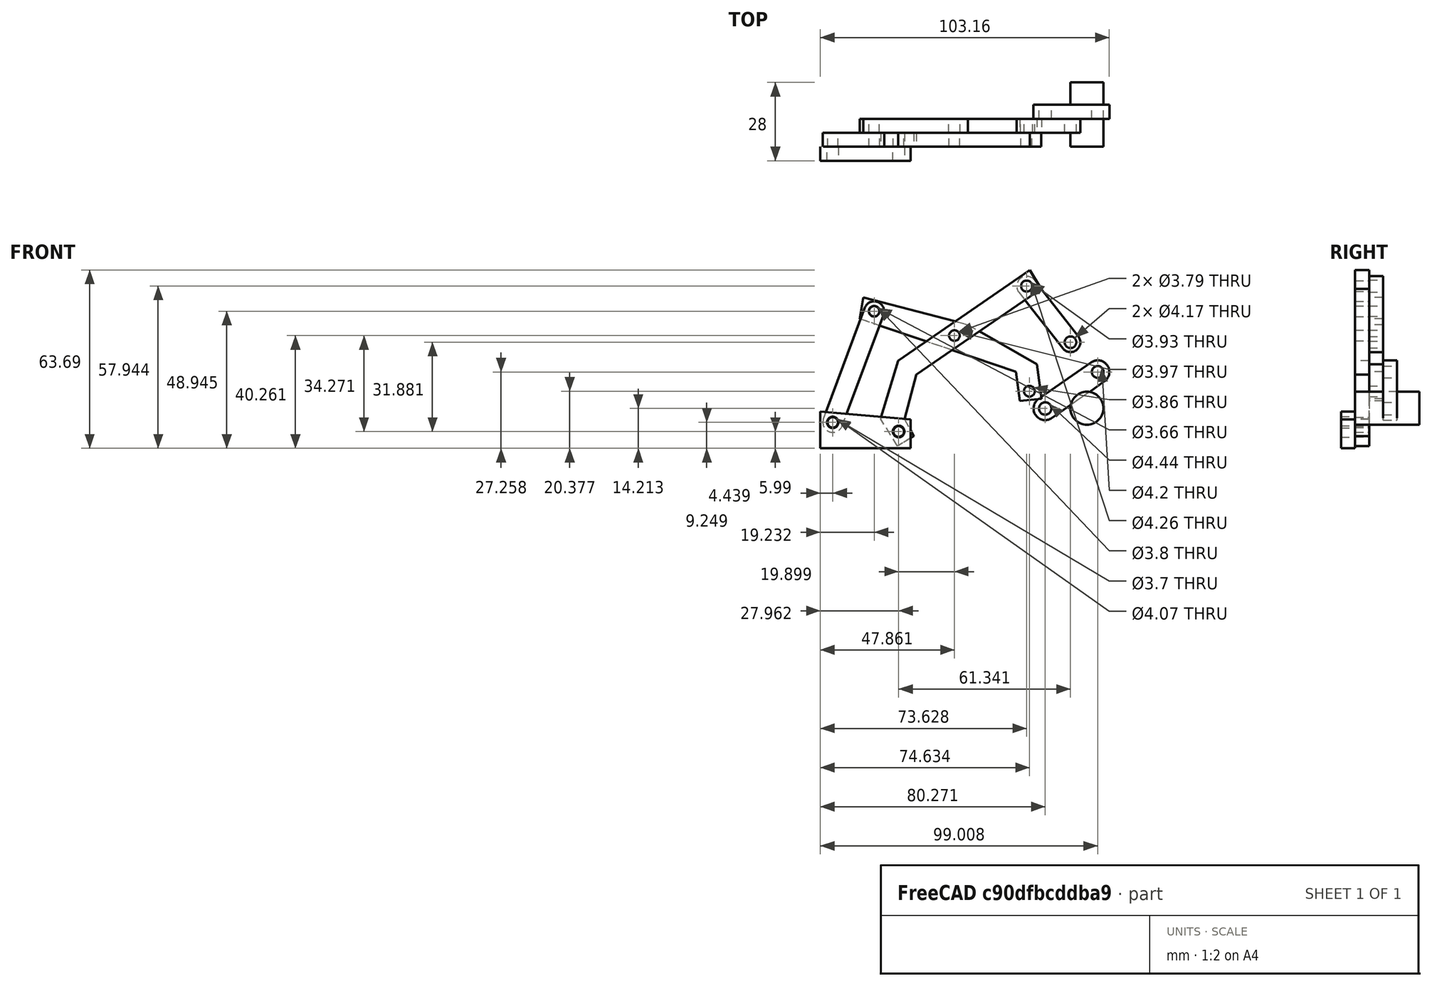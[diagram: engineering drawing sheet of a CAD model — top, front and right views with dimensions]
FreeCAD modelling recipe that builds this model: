
FCSTD DOCUMENT  (FreeCAD 1.1R14555 (Git shallow))
Label: TestMeca1-1
License: All rights reserved
LicenseURL: https://en.wikipedia.org/wiki/All_rights_reserved
objects: App::Point×11, App::FeaturePython×10, Sketcher::SketchObject×7, PartDesign::Pad×7, PartDesign::Body×7, App::Link×4, Assembly::JointGroup×2, Assembly::AssemblyObject×2, Image::ImagePlane×1, App::Part×1, Assembly::AssemblyLink×1
note: 42 computed .brp shape members not serialized (recipe doc carries the construction recipe); baked Part::Feature solids carry a one-line shape summary decoded from their .brp
EXTERNAL_REF file=TestInsert1-1.FCStd obj=Assembly
EXTERNAL_REF file=TestInsert1-1.FCStd obj=Body
EXTERNAL_REF file=TestInsert1-1.FCStd obj=Body001

FEATURE [App::Point] Origin001  label="Origine"
  Role = Origin
FEATURE [Image::ImagePlane] GN_7247_Charnière_articulée_drawing  label="GN 7247-Charnière articulée-drawing"
  Placement = pos=(-46,0,-26) rot=(1,0,0;1.5708rad)
  XSize = 264.55
  YSize = 264.55
FEATURE [App::Point] Origin003  label="Origine002"
  Role = Origin
FEATURE [Sketcher::SketchObject] Sketch
  ArcFitTolerance = 1e-06
  AttachmentSupport = -> [Origin002]
  ExternalTypes = [0]
  FullyConstrained = false
  MakeInternals = false
  MapMode = 5
  Placement = pos=(0,0,0) rot=(1,0,0;1.5708rad)
  sketch-geometry (6):
    g0: LineSegment StartX=0 StartY=0 StartZ=0 EndX=0 EndY=13.138 EndZ=0
    g1: LineSegment StartX=0 StartY=13.138 StartZ=0 EndX=32.2081 EndY=10.2743 EndZ=0
    g2: LineSegment StartX=32.2081 StartY=10.2743 StartZ=0 EndX=32.2081 EndY=0 EndZ=0
    g3: LineSegment StartX=32.2081 StartY=0 StartZ=0 EndX=0 EndY=0 EndZ=0
    g4: Circle CenterX=27.9622 CenterY=5.98985 CenterZ=0 NormalX=0 NormalY=0 NormalZ=1 AngleXU=0 Radius=2.08292
    g5: Circle CenterX=4.43862 CenterY=9.24882 CenterZ=0 NormalX=0 NormalY=0 NormalZ=1 AngleXU=0 Radius=2.03403
  constraints (8):
    c: Coincident(g-1,g0)
    c: PointOnObject(g0,g-2)
    c: Coincident(g0,g1)
    c: Coincident(g1,g2)
    c: PointOnObject(g2,g-1)
    c: Vertical(g2)
    c: Coincident(g2,g3)
    c: Coincident(g3,g0)
FEATURE [PartDesign::Pad] Pad
  Direction = (0,-1,0)
  Length = 5
  Length2 = 10
  Profile = -> Sketch
  ReferenceAxis = -> Sketch [N_Axis]
  Refine = true
  SideType = 0
  Suppressed = false
  Type = 0
  Type2 = 0
FEATURE [PartDesign::Body] Body  label="Corps"
  AllowCompound = false
  Group = -> [Sketch,Pad]
  Origin = -> Origin002
  Tip = -> Pad
FEATURE [App::Point] Origin005  label="Origine004"
  Role = Origin
FEATURE [Sketcher::SketchObject] Sketch001
  ArcFitTolerance = 1e-06
  AttachmentSupport = -> [Origin004]
  ExternalTypes = [0]
  FullyConstrained = false
  MakeInternals = false
  MapMode = 5
  Placement = pos=(0,0,0) rot=(1,0,0;1.5708rad)
  sketch-geometry (6):
    g0: ArcOfCircle CenterX=4.3933 CenterY=9.28745 CenterZ=0 NormalX=0 NormalY=0 NormalZ=1 AngleXU=0 Radius=3.55115 StartAngle=3.65377 EndAngle=6.79537
    g1: ArcOfCircle CenterX=-16.3679 CenterY=46.2142 CenterZ=0 NormalX=0 NormalY=0 NormalZ=1 AngleXU=0 Radius=3.55115 StartAngle=0.512182 EndAngle=3.65377
    g2: LineSegment StartX=1.29784 StartY=7.5471 StartZ=0 EndX=-19.4634 EndY=44.4739 EndZ=0
    g3: LineSegment StartX=7.48876 StartY=11.0278 StartZ=0 EndX=-13.2724 EndY=47.9545 EndZ=0
    g4: Circle CenterX=-16.3679 CenterY=46.2142 CenterZ=0 NormalX=0 NormalY=0 NormalZ=1 AngleXU=0 Radius=1.89824
    g5: Circle CenterX=4.3933 CenterY=9.28745 CenterZ=0 NormalX=0 NormalY=0 NormalZ=1 AngleXU=0 Radius=1.85066
  constraints (7):
    c: Tangent(g0,g2) = 1.5708
    c: Tangent(g0,g3) = -1.5708
    c: Tangent(g1,g2) = 1.5708
    c: Tangent(g1,g3) = -1.5708
    c: Equal(g0,g1)
    c: Coincident(g4,g1)
    c: Coincident(g5,g0)
FEATURE [PartDesign::Pad] Pad001
  Direction = (0,-1,2e-16)
  Length = 5
  Length2 = 10
  Profile = -> Sketch001
  ReferenceAxis = -> Sketch001 [N_Axis]
  Refine = true
  SideType = 0
  Suppressed = false
  Type = 0
  Type2 = 0
FEATURE [PartDesign::Body] Body001  label="Corps001"
  AllowCompound = false
  Group = -> [Sketch001,Pad001]
  Origin = -> Origin004
  Placement = pos=(-5.49004,5,6.60695) rot=(0,1,0;0.868892rad)
  Tip = -> Pad001
FEATURE [App::Point] Origin007  label="Origine006"
  Role = Origin
FEATURE [Sketcher::SketchObject] Sketch002
  ArcFitTolerance = 1e-06
  AttachmentSupport = -> [Origin006]
  ExternalTypes = [0]
  FullyConstrained = false
  MakeInternals = false
  MapMode = 5
  Placement = pos=(0,0,0) rot=(1,0,0;1.5708rad)
  sketch-geometry (6):
    g0: ArcOfCircle CenterX=9.93968 CenterY=74.2901 CenterZ=0 NormalX=0 NormalY=0 NormalZ=1 AngleXU=0 Radius=3.51304 StartAngle=0.499119 EndAngle=3.64071
    g1: ArcOfCircle CenterX=22.1303 CenterY=51.9285 CenterZ=0 NormalX=0 NormalY=0 NormalZ=1 AngleXU=0 Radius=3.51304 StartAngle=3.64071 EndAngle=6.7823
    g2: LineSegment StartX=13.0241 StartY=75.9716 StartZ=0 EndX=25.2148 EndY=53.61 EndZ=0
    g3: LineSegment StartX=6.85522 StartY=72.6086 StartZ=0 EndX=19.0458 EndY=50.247 EndZ=0
    g4: Circle CenterX=9.93968 CenterY=74.2901 CenterZ=0 NormalX=0 NormalY=0 NormalZ=1 AngleXU=0 Radius=2.12816
    g5: Circle CenterX=22.1303 CenterY=51.9285 CenterZ=0 NormalX=0 NormalY=0 NormalZ=1 AngleXU=0 Radius=2.08513
  constraints (7):
    c: Tangent(g0,g2) = 1.5708
    c: Tangent(g0,g3) = -1.5708
    c: Tangent(g1,g2) = 1.5708
    c: Tangent(g1,g3) = -1.5708
    c: Equal(g0,g1)
    c: Coincident(g4,g0)
    c: Coincident(g5,g1)
FEATURE [PartDesign::Pad] Pad002
  Direction = (0,-1,2e-16)
  Length = 5
  Length2 = 10
  Profile = -> Sketch002
  ReferenceAxis = -> Sketch002 [N_Axis]
  Refine = true
  SideType = 0
  Suppressed = false
  Type = 0
  Type2 = 0
FEATURE [PartDesign::Body] Body002  label="Corps002"
  AllowCompound = false
  Group = -> [Sketch002,Pad002]
  Origin = -> Origin006
  Placement = pos=(75.9415,10,-16.972) rot=(0,-1,0;0.16388rad)
  Tip = -> Pad002
FEATURE [App::Point] Origin009  label="Origine008"
  Role = Origin
FEATURE [Sketcher::SketchObject] Sketch003
  ArcFitTolerance = 1e-06
  AttachmentSupport = -> [Origin008]
  ExternalTypes = [0]
  FullyConstrained = false
  MakeInternals = false
  MapMode = 5
  Placement = pos=(0,0,0) rot=(1,0,0;1.5708rad)
  sketch-geometry (6):
    g0: ArcOfCircle CenterX=33.0045 CenterY=40.5366 CenterZ=0 NormalX=0 NormalY=0 NormalZ=1 AngleXU=0 Radius=4.15593 StartAngle=1e-16 EndAngle=3.14159
    g1: ArcOfCircle CenterX=33.0045 CenterY=17.7064 CenterZ=0 NormalX=0 NormalY=0 NormalZ=1 AngleXU=0 Radius=4.15593 StartAngle=3.14159 EndAngle=6.28319
    g2: LineSegment StartX=37.1605 StartY=40.5366 StartZ=0 EndX=37.1605 EndY=17.7064 EndZ=0
    g3: LineSegment StartX=28.8486 StartY=40.5366 StartZ=0 EndX=28.8486 EndY=17.7064 EndZ=0
    g4: Circle CenterX=33.0045 CenterY=40.5366 CenterZ=0 NormalX=0 NormalY=0 NormalZ=1 AngleXU=0 Radius=2.09794
    g5: Circle CenterX=33.0045 CenterY=17.7064 CenterZ=0 NormalX=0 NormalY=0 NormalZ=1 AngleXU=0 Radius=2.22145
  constraints (8):
    c: Tangent(g0,g2) = 1.5708
    c: Tangent(g0,g3) = -1.5708
    c: Tangent(g1,g2) = 1.5708
    c: Tangent(g1,g3) = -1.5708
    c: Equal(g0,g1)
    c: Vertical(g2)
    c: Coincident(g4,g0)
    c: Coincident(g5,g1)
FEATURE [PartDesign::Pad] Pad003
  Direction = (0,-1,0)
  Length = 5
  Length2 = 10
  Profile = -> Sketch003
  ReferenceAxis = -> Sketch003 [N_Axis]
  Refine = true
  SideType = 0
  Suppressed = false
  Type = 0
  Type2 = 0
FEATURE [PartDesign::Body] Body003  label="Corps003"
  AllowCompound = false
  Group = -> [Sketch003,Pad003]
  Origin = -> Origin008
  Placement = pos=(46.8816,15,31.1819) rot=(0,1,0;0.962596rad)
  Tip = -> Pad003
FEATURE [App::Point] Origin011  label="Origine010"
  Role = Origin
FEATURE [Sketcher::SketchObject] Sketch004
  ArcFitTolerance = 1e-06
  AttachmentSupport = -> [Origin010]
  ExternalTypes = [0]
  FullyConstrained = false
  MakeInternals = false
  MapMode = 5
  Placement = pos=(0,0,0) rot=(1,0,0;1.5708rad)
  sketch-geometry (10):
    g0: LineSegment StartX=-23.6072 StartY=51.3966 StartZ=0 EndX=-21.2757 EndY=58.8351 EndZ=0
    g1: LineSegment StartX=-21.2757 StartY=58.8351 StartZ=0 EndX=14.4735 EndY=44.1801 EndZ=0
    g2: LineSegment StartX=14.4735 StartY=44.1801 StartZ=0 EndX=37.011 EndY=26.9717 EndZ=0
    g3: LineSegment StartX=37.011 StartY=26.9717 StartZ=0 EndX=37.011 EndY=14.5372 EndZ=0
    g4: LineSegment StartX=37.011 StartY=14.5372 StartZ=0 EndX=29.2394 EndY=14.8702 EndZ=0
    g5: LineSegment StartX=29.2394 StartY=14.8702 StartZ=0 EndX=29.2394 EndY=25.3063 EndZ=0
    g6: LineSegment StartX=29.2394 StartY=25.3063 StartZ=0 EndX=-23.6072 EndY=51.3966 EndZ=0
    g7: Circle CenterX=33.061 CenterY=17.7892 CenterZ=0 NormalX=0 NormalY=0 NormalZ=1 AngleXU=0 Radius=1.92887
    g8: Circle CenterX=9.13695 CenterY=41.0232 CenterZ=0 NormalX=0 NormalY=0 NormalZ=1 AngleXU=0 Radius=1.9865
    g9: Circle CenterX=-18.1003 CenterY=53.3997 CenterZ=0 NormalX=0 NormalY=0 NormalZ=1 AngleXU=0 Radius=1.8317
  constraints (9):
    c: Coincident(g0,g1)
    c: Coincident(g1,g2)
    c: Coincident(g2,g3)
    c: Vertical(g3)
    c: Coincident(g3,g4)
    c: Coincident(g4,g5)
    c: Vertical(g5)
    c: Coincident(g5,g6)
    c: Coincident(g6,g0)
FEATURE [PartDesign::Pad] Pad004
  Direction = (0,-1,0)
  Length = 5
  Length2 = 10
  Profile = -> Sketch004
  ReferenceAxis = -> Sketch004 [N_Axis]
  Refine = true
  SideType = 0
  Suppressed = false
  Type = 0
  Type2 = 0
FEATURE [PartDesign::Body] Body004  label="Corps004"
  AllowCompound = false
  Group = -> [Sketch004,Pad004]
  Origin = -> Origin010
  Placement = pos=(44.202,10,-1.60818) rot=(0,-1,0;0.131988rad)
  Tip = -> Pad004
FEATURE [App::Point] Origin013  label="Origine012"
  Role = Origin
FEATURE [Sketcher::SketchObject] Sketch005
  ArcFitTolerance = 1e-06
  AttachmentSupport = -> [Origin012]
  ExternalTypes = [0]
  FullyConstrained = false
  MakeInternals = false
  MapMode = 5
  Placement = pos=(0,0,0) rot=(1,0,0;1.5708rad)
  sketch-geometry (11):
    g0: LineSegment StartX=3.31041 StartY=76.0954 StartZ=0 EndX=11.193 EndY=76.0954 EndZ=0
    g1: LineSegment StartX=11.193 StartY=76.0954 StartZ=0 EndX=13.8575 EndY=22.0275 EndZ=0
    g2: LineSegment StartX=13.8575 StartY=22.0275 StartZ=0 EndX=25.3278 EndY=10.0553 EndZ=0
    g3: LineSegment StartX=25.3278 StartY=10.0553 StartZ=0 EndX=32.1894 EndY=9.81025 EndZ=0
    g4: LineSegment StartX=32.1894 StartY=9.81025 StartZ=0 EndX=32.1894 EndY=2.90781 EndZ=0
    g5: LineSegment StartX=32.1894 StartY=2.90781 StartZ=0 EndX=20.7126 EndY=2.90781 EndZ=0
    g6: LineSegment StartX=20.7126 StartY=2.90781 StartZ=0 EndX=6.25418 EndY=19.1224 EndZ=0
    g7: LineSegment StartX=6.25418 StartY=19.1224 StartZ=0 EndX=3.31041 EndY=76.0954 EndZ=0
    g8: Circle CenterX=7.62181 CenterY=72.1475 CenterZ=0 NormalX=0 NormalY=0 NormalZ=1 AngleXU=0 Radius=1.96538
    g9: Circle CenterX=9.17842 CenterY=40.9348 CenterZ=0 NormalX=0 NormalY=0 NormalZ=1 AngleXU=0 Radius=1.89735
    g10: Circle CenterX=27.9374 CenterY=6.02718 CenterZ=0 NormalX=0 NormalY=0 NormalZ=1 AngleXU=0 Radius=1.89735
  constraints (11):
    c: Horizontal(g0)
    c: Coincident(g0,g1)
    c: Coincident(g1,g2)
    c: Coincident(g2,g3)
    c: Coincident(g3,g4)
    c: Vertical(g4)
    c: Coincident(g4,g5)
    c: Horizontal(g5)
    c: Coincident(g5,g6)
    c: Coincident(g6,g7)
    c: Coincident(g7,g0)
FEATURE [PartDesign::Pad] Pad005
  Direction = (0,-1,0)
  Length = 5
  Length2 = 10
  Profile = -> Sketch005
  ReferenceAxis = -> Sketch005 [N_Axis]
  Refine = true
  SideType = 0
  Suppressed = false
  Type = 0
  Type2 = 0
FEATURE [PartDesign::Body] Body005  label="Corps005"
  AllowCompound = false
  Group = -> [Sketch005,Pad005]
  Origin = -> Origin012
  Placement = pos=(8.18757,5,26.6245) rot=(0,1,0;1.01916rad)
  Tip = -> Pad005
FEATURE [App::FeaturePython] GroundedJoint  # Assembly grounded joint (typed FeaturePython)
  ObjectToGround = -> Body
FEATURE [App::FeaturePython] Joint  label="Revolute"  # Assembly joint (typed FeaturePython)
  Angle = 0
  AngleMax = 0
  AngleMin = 0
  Detach1 = false
  Detach2 = false
  Distance = 0
  Distance2 = 0
  EnableAngleMax = false
  EnableAngleMin = false
  EnableLengthMax = false
  EnableLengthMin = false
  JointType = 1 (Revolute)
  LengthMax = 0
  LengthMin = 0
  Placement1 = pos=(4.3933,-5,9.28745) rot=(1,0,0;1.5708rad)
  Placement2 = pos=(4.43862,0,9.24882) rot=(1,0,0;1.5708rad)
  Reference1 = -> Assembly [Body001.Edge18,Body001.Edge18]
  Reference2 = -> Assembly [Body.Edge17,Body.Edge17]
  Suppressed = false
FEATURE [App::FeaturePython] Joint001  label="Revolute001"  # Assembly joint (typed FeaturePython)
  Angle = 0
  AngleMax = 0
  AngleMin = 0
  Detach1 = false
  Detach2 = false
  Distance = 0
  Distance2 = 0
  EnableAngleMax = false
  EnableAngleMin = false
  EnableLengthMax = false
  EnableLengthMin = false
  JointType = 1 (Revolute)
  LengthMax = 0
  LengthMin = 0
  Placement1 = pos=(-16.3679,0,46.2142) rot=(1,0,0;1.5708rad)
  Placement2 = pos=(-18.1003,-5,53.3997) rot=(1,0,0;1.5708rad)
  Reference1 = -> Assembly [Body001.Edge14,Body001.Edge14]
  Reference2 = -> Assembly [Body004.Edge30,Body004.Edge30]
  Suppressed = false
FEATURE [App::FeaturePython] Joint002  label="Revolute002"  # Assembly joint (typed FeaturePython)
  Angle = 0
  AngleMax = 0
  AngleMin = 0
  Detach1 = false
  Detach2 = false
  Distance = 0
  Distance2 = 0
  EnableAngleMax = false
  EnableAngleMin = false
  EnableLengthMax = false
  EnableLengthMin = false
  JointType = 1 (Revolute)
  LengthMax = 0
  LengthMin = 0
  Placement1 = pos=(27.9374,-5,6.02718) rot=(1,0,0;1.5708rad)
  Placement2 = pos=(27.9622,0,5.98985) rot=(1,0,0;1.5708rad)
  Reference1 = -> Assembly [Body005.Edge33,Body005.Edge33]
  Reference2 = -> Assembly [Body.Edge14,Body.Edge14]
  Suppressed = false
FEATURE [App::FeaturePython] Joint005  label="Revolute005"  # Assembly joint (typed FeaturePython)
  Angle = 0
  AngleMax = 0
  AngleMin = 0
  Detach1 = false
  Detach2 = false
  Distance = 0
  Distance2 = 0
  EnableAngleMax = false
  EnableAngleMin = false
  EnableLengthMax = false
  EnableLengthMin = false
  JointType = 1 (Revolute)
  LengthMax = 0
  LengthMin = 0
  Placement1 = pos=(9.93968,-5,74.2901) rot=(1,0,0;1.5708rad)
  Placement2 = pos=(7.62181,0,72.1475) rot=(1,0,0;1.5708rad)
  Reference1 = -> Assembly [Body002.Edge15,Body002.Edge15]
  Reference2 = -> Assembly [Body005.Edge26,Body005.Edge26]
  Suppressed = false
FEATURE [App::FeaturePython] Joint006  label="Revolute006"  # Assembly joint (typed FeaturePython)
  Angle = 0
  AngleMax = 0
  AngleMin = 0
  Detach1 = false
  Detach2 = false
  Distance = 0
  Distance2 = 0
  EnableAngleMax = false
  EnableAngleMin = false
  EnableLengthMax = false
  EnableLengthMin = false
  JointType = 1 (Revolute)
  LengthMax = 0
  LengthMin = 0
  Placement1 = pos=(9.13695,-5,41.0232) rot=(1,0,0;1.5708rad)
  Placement2 = pos=(9.17842,0,40.9348) rot=(1,0,0;1.5708rad)
  Reference1 = -> Assembly [Body004.Edge24,Body004.Edge24]
  Reference2 = -> Assembly [Body005.Edge29,Body005.Edge29]
  Suppressed = false
FEATURE [App::Point] Origin015  label="Origine014"
  Role = Origin
FEATURE [App::Point] Origin017  label="Origine016"
  Role = Origin
FEATURE [Sketcher::SketchObject] Sketch006
  ArcFitTolerance = 1e-06
  AttachmentSupport = -> [Origin016]
  ExternalTypes = [0]
  FullyConstrained = false
  MakeInternals = false
  MapMode = 5
  Placement = pos=(0,0,0) rot=(1,0,0;1.5708rad)
  sketch-geometry (1):
    g0: Circle CenterX=95.172 CenterY=14.315 CenterZ=0 NormalX=0 NormalY=0 NormalZ=1 AngleXU=0 Radius=5.91026
FEATURE [PartDesign::Pad] Pad006
  Direction = (0,-1,2e-16)
  Length = 23
  Length2 = 10
  Profile = -> Sketch006
  ReferenceAxis = -> Sketch006 [N_Axis]
  Refine = true
  Reversed = true
  SideType = 0
  Suppressed = false
  Type = 0
  Type2 = 0
FEATURE [PartDesign::Body] Body006  label="Corps006"
  AllowCompound = false
  Group = -> [Sketch006,Pad006]
  Origin = -> Origin016
  Tip = -> Pad006
FEATURE [App::Part] Part
  Group = -> [Body003,Body006]
  Origin = -> Origin014
FEATURE [App::Point] Origin019  label="Origine018"
  Role = Origin
FEATURE [App::Link] Corps003
  LinkPlacement = pos=(77,-8.82149e-06,-4.76837e-07) rot=(0,0,1;0rad)
  LinkedObject = -> Body003
  Placement = pos=(77,-8.82149e-06,-4.76837e-07) rot=(0,0,1;0rad)
FEATURE [App::Link] Corps006
  LinkPlacement = pos=(14.8325,-13,14.8956) rot=(0,0,1;0rad)
  LinkedObject = -> Body006
  Placement = pos=(14.8325,-13,14.8956) rot=(0,0,1;0rad)
FEATURE [App::FeaturePython] Joint007  label="Fixed001"  # Assembly joint (typed FeaturePython)
  Angle = 0
  AngleMax = 0
  AngleMin = 0
  Detach1 = false
  Detach2 = false
  Distance = 0
  Distance2 = 0
  EnableAngleMax = false
  EnableAngleMin = false
  EnableLengthMax = false
  EnableLengthMin = false
  JointType = 0 (Fixed)
  LengthMax = 0
  LengthMin = 0
  Offset2 = pos=(0,0,-8) rot=(0,0,1;0rad)
  Placement1 = pos=(95.172,3.6e-15,14.315) rot=(0.57735,0.57735,0.57735;4.18879rad)
  Placement2 = pos=(33.0045,-13,29.2106) rot=(0.57735,0.57735,0.57735;4.18879rad)
  Reference1 = -> Assembly [Assembly001.Corps006.Face2,Assembly001.Corps006.Face2]
  Reference2 = -> Assembly [Assembly001.Corps003.Face8,Assembly001.Corps003.Face8]
  Suppressed = false
FEATURE [Assembly::JointGroup] Joints001
  Group = -> [Joint007]
FEATURE [Assembly::AssemblyObject] Assembly001
  Group = -> [Joints001,Corps003,Corps006,Joint007]
  Origin = -> Origin018
  Placement = pos=(-21.035,5.00001,77.4903) rot=(0,1,0;0.697791rad)
  Type = Assembly
FEATURE [App::FeaturePython] Joint008  label="Revolute011"  # Assembly joint (typed FeaturePython)
  Angle = 0
  AngleMax = 0
  AngleMin = 0
  Detach1 = false
  Detach2 = false
  Distance = 0
  Distance2 = 0
  EnableAngleMax = false
  EnableAngleMin = false
  EnableLengthMax = false
  EnableLengthMin = false
  JointType = 1 (Revolute)
  LengthMax = 0
  LengthMin = 0
  Placement1 = pos=(33.0045,0,40.5366) rot=(1,0,0;1.5708rad)
  Placement2 = pos=(22.1303,-5,51.9285) rot=(1,0,0;1.5708rad)
  Reference1 = -> Assembly [Assembly001.Corps003.Edge17,Assembly001.Corps003.Edge17]
  Reference2 = -> Assembly [Body002.Edge18,Body002.Edge18]
  Suppressed = false
FEATURE [App::FeaturePython] Joint009  label="Revolute012"  # Assembly joint (typed FeaturePython)
  Angle = 0
  AngleMax = 0
  AngleMin = 0
  Detach1 = false
  Detach2 = false
  Distance = 0
  Distance2 = 0
  EnableAngleMax = false
  EnableAngleMin = false
  EnableLengthMax = false
  EnableLengthMin = false
  JointType = 1 (Revolute)
  LengthMax = 0
  LengthMin = 0
  Placement1 = pos=(33.0045,0,17.7064) rot=(1,0,0;1.5708rad)
  Placement2 = pos=(33.061,-5,17.7892) rot=(1,0,0;1.5708rad)
  Reference1 = -> Assembly [Assembly001.Corps003.Edge14,Assembly001.Corps003.Edge14]
  Reference2 = -> Assembly [Body004.Edge27,Body004.Edge27]
  Suppressed = false
FEATURE [App::Point] Origin021  label="Origine020"
  Role = Origin
FEATURE [App::Link] Body007  label="Corps007"
  LinkedObject = -> <external TestInsert1-1.FCStd>#Body
FEATURE [App::Link] Body008  label="Corps008"
  LinkPlacement = pos=(-4.1e-15,3.6e-15,-4.7e-15) rot=(0,-1,0;4.71239rad)
  LinkedObject = -> <external TestInsert1-1.FCStd>#Body001
  Placement = pos=(-4.1e-15,3.6e-15,-4.7e-15) rot=(0,-1,0;4.71239rad)
FEATURE [Assembly::AssemblyLink] Assembly002  label="Assembly"
  Group = -> [Body007,Body008]
  LinkedObject = -> <external TestInsert1-1.FCStd>#Assembly
  Origin = -> Origin020
  Placement = pos=(82.0261,-8,29.1925) rot=(0,1,0;0.730396rad)
  Rigid = true
FEATURE [App::FeaturePython] Joint010  label="Revolute014"  # Assembly joint (typed FeaturePython)
  Angle = 0
  AngleMax = 0
  AngleMin = 0
  Detach1 = false
  Detach2 = false
  Distance = 0
  Distance2 = 0
  EnableAngleMax = false
  EnableAngleMin = false
  EnableLengthMax = false
  EnableLengthMin = false
  JointType = 1 (Revolute)
  LengthMax = 0
  LengthMin = 0
  Placement1 = pos=(0,0,0) rot=(-1,0,0;4.71239rad)
  Placement2 = pos=(95.172,0,14.315) rot=(1,0,0;1.5708rad)
  Reference1 = -> Assembly [Assembly002.Body008.Edge2,Assembly002.Body008.Edge2]
  Reference2 = -> Assembly [Assembly001.Corps006.Edge2,Assembly001.Corps006.Edge2]
  Suppressed = false
FEATURE [Assembly::JointGroup] Joints
  Group = -> [GroundedJoint,Joint,Joint001,Joint002,Joint005,Joint006,Joint008,Joint009,Joint010]
FEATURE [Assembly::AssemblyObject] Assembly
  Group = -> [Joints,Body,Body001,Body002,Body004,Body005,GroundedJoint,Joint,Joint001,Joint002,Joint005,Joint006,Assembly001,Joint008,Joint009,Assembly002,Joint010]
  Origin = -> Origin
  Type = Assembly

RESOLVED EXTERNAL PARTS (link-assembly join: the EXTERNAL_REF files above that resolve inside this repo's crawl, each included once):
---- part TestInsert1-1.FCStd = doc fcstd_bb9fa522eb82 ----
FCSTD DOCUMENT  (FreeCAD 1.1R14555 (Git shallow))
Label: TestInsert1-1
License: All rights reserved
LicenseURL: https://en.wikipedia.org/wiki/All_rights_reserved
objects: App::Point×3, Sketcher::SketchObject×2, PartDesign::Pad×2, PartDesign::Body×2, App::FeaturePython×1, Assembly::JointGroup×1, Assembly::AssemblyObject×1
note: 12 computed .brp shape members not serialized (recipe doc carries the construction recipe); baked Part::Feature solids carry a one-line shape summary decoded from their .brp

FEATURE [App::Point] Origin001  label="Origine"
  Role = Origin
FEATURE [App::Point] Origin003  label="Origine002"
  Role = Origin
FEATURE [Sketcher::SketchObject] Sketch
  ArcFitTolerance = 1e-06
  AttachmentSupport = -> [Origin002]
  ExternalTypes = [0]
  FullyConstrained = false
  MakeInternals = false
  MapMode = 5
  Placement = pos=(0,0,0) rot=(1,0,0;1.5708rad)
  sketch-geometry (4):
    g0: ArcOfCircle CenterX=0 CenterY=0 CenterZ=0 NormalX=0 NormalY=0 NormalZ=1 AngleXU=0 Radius=3.30838 StartAngle=2.28574 EndAngle=5.42733
    g1: ArcOfCircle CenterX=11.4427 CenterY=9.93411 CenterZ=0 NormalX=0 NormalY=0 NormalZ=1 AngleXU=0 Radius=3.30838 StartAngle=5.42733 EndAngle=8.56893
    g2: LineSegment StartX=-2.1689 StartY=2.49826 StartZ=0 EndX=9.27378 EndY=12.4324 EndZ=0
    g3: LineSegment StartX=2.1689 StartY=-2.49826 StartZ=0 EndX=13.6116 EndY=7.43585 EndZ=0
  constraints (6):
    c: Tangent(g0,g2) = 1.5708
    c: Tangent(g0,g3) = -1.5708
    c: Tangent(g1,g2) = 1.5708
    c: Tangent(g1,g3) = -1.5708
    c: Equal(g0,g1)
    c: Coincident(g0,g-1)
FEATURE [PartDesign::Pad] Pad
  Direction = (0,-1,0)
  Length = 10
  Length2 = 10
  Profile = -> Sketch
  ReferenceAxis = -> Sketch [N_Axis]
  Refine = true
  SideType = 0
  Suppressed = false
  Type = 0
  Type2 = 0
FEATURE [PartDesign::Body] Body  label="Corps"
  AllowCompound = false
  Group = -> [Sketch,Pad]
  Origin = -> Origin002
  Tip = -> Pad
FEATURE [App::Point] Origin005  label="Origine004"
  Role = Origin
FEATURE [Sketcher::SketchObject] Sketch001
  ArcFitTolerance = 1e-06
  AttachmentSupport = -> [Origin004]
  ExternalTypes = [0]
  FullyConstrained = false
  MakeInternals = false
  MapMode = 5
  Placement = pos=(0,0,0) rot=(1,0,0;1.5708rad)
  sketch-geometry (1):
    g0: Circle CenterX=0 CenterY=0 CenterZ=0 NormalX=0 NormalY=0 NormalZ=1 AngleXU=0 Radius=7.06658
  constraints (1):
    c: Coincident(g0,g-1)
FEATURE [PartDesign::Pad] Pad001
  Direction = (0,-1,0)
  Length = 10
  Length2 = 10
  Profile = -> Sketch001
  ReferenceAxis = -> Sketch001 [N_Axis]
  Refine = true
  SideType = 0
  Suppressed = false
  Type = 0
  Type2 = 0
FEATURE [PartDesign::Body] Body001  label="Corps001"
  AllowCompound = false
  Group = -> [Sketch001,Pad001]
  Origin = -> Origin004
  Placement = pos=(-4.1e-15,3.6e-15,-4.7e-15) rot=(0,-1,0;4.71239rad)
  Tip = -> Pad001
FEATURE [App::FeaturePython] Joint  label="Fixed"  # Assembly joint (typed FeaturePython)
  Angle = 0
  AngleMax = 0
  AngleMin = 0
  Detach1 = false
  Detach2 = false
  Distance = 0
  Distance2 = 0
  EnableAngleMax = false
  EnableAngleMin = false
  EnableLengthMax = false
  EnableLengthMin = false
  JointType = 0 (Fixed)
  LengthMax = 0
  LengthMin = 0
  Placement1 = pos=(9e-16,-10,2.2e-15) rot=(0.57735,0.57735,0.57735;4.18879rad)
  Placement2 = pos=(0,-10,2.2e-15) rot=(1,0,0;1.5708rad)
  Reference1 = -> Assembly [Body001.Face3,Body001.Face3]
  Reference2 = -> Assembly [Body.Edge4,Body.Edge4]
  Suppressed = false
FEATURE [Assembly::JointGroup] Joints
  Group = -> [Joint]
FEATURE [Assembly::AssemblyObject] Assembly
  Group = -> [Joints,Body,Body001,Joint]
  Origin = -> Origin
  Type = Assembly
